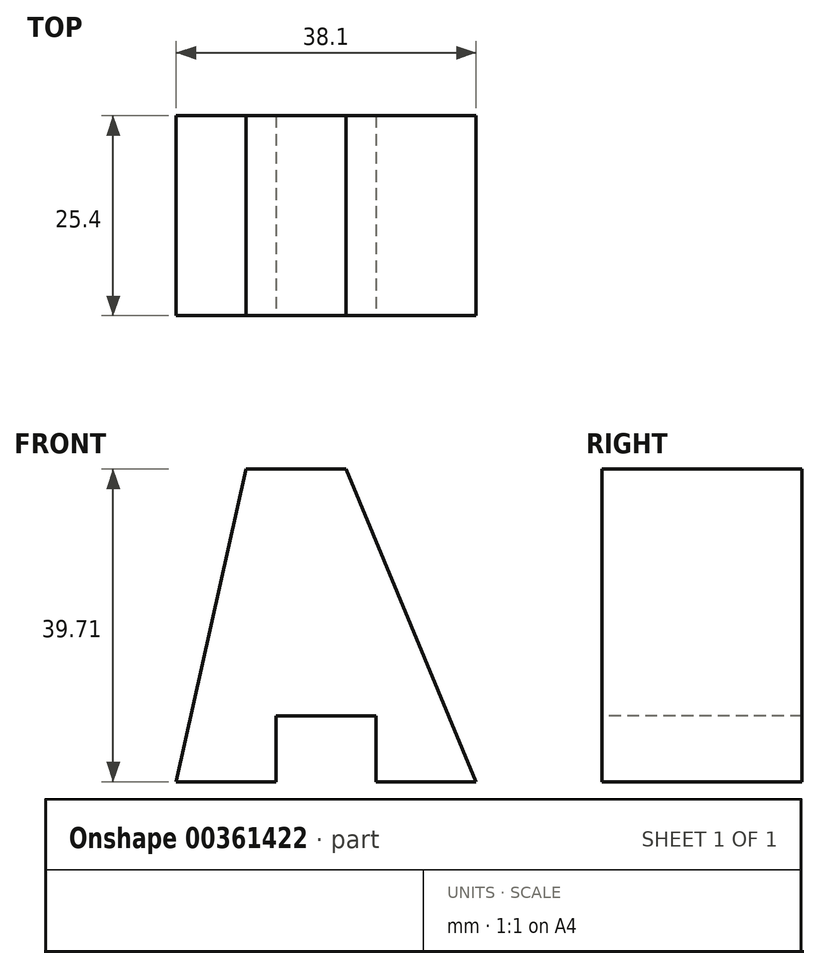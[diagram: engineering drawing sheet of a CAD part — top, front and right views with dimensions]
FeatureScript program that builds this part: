
annotation { "Feature Type Name" : "Feature", "Feature Type Description" : "" }
export const myFeature = defineFeature(function(context is Context, id is Id, definition is map)
    precondition{}
    {
        {
            var Q0;
            Q0=qCreatedBy(makeId("Front.planeOp"),FACE);
            var sketch = newSketch(context, id + "F0", { "sketchPlane" : qUnion([Q0])});
            skLineSegment(sketch, "E0", {"start": v(38.1, 0) * mm, "end": v(21.55, 39.71) * mm});
            skLineSegment(sketch, "E1", {"start": v(21.55, 39.71) * mm, "end": v(8.85, 39.71) * mm});
            skLineSegment(sketch, "E2", {"start": v(8.85, 39.71) * mm, "end": v(0, 0) * mm});
            skLineSegment(sketch, "E3", {"start": v(0, 0) * mm, "end": v(12.7, 0) * mm});
            skLineSegment(sketch, "E4", {"start": v(12.7, 0) * mm, "end": v(12.7, 8.37) * mm});
            skLineSegment(sketch, "E5", {"start": v(12.7, 8.37) * mm, "end": v(25.4, 8.37) * mm});
            skLineSegment(sketch, "E6", {"start": v(25.4, 8.37) * mm, "end": v(25.4, 0) * mm});
            skLineSegment(sketch, "E7", {"start": v(25.4, 0) * mm, "end": v(38.1, 0) * mm});
            skSolve(sketch);
        }
        {
            var Q0;
            Q0 = qSketchRegion(id + "F0", true);
            extrude(context, id + "F1", {"entities" : qUnion([Q0]), "oppositeDirection" : true, "depth" : 25.4 * mm});
        }
    });
